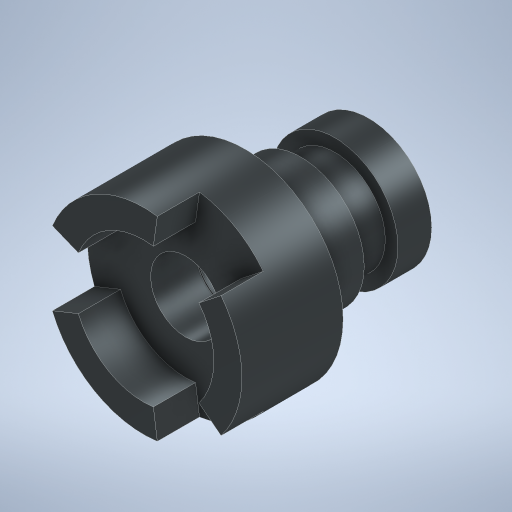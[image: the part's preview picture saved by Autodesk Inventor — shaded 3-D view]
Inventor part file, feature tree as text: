
AUTODESK INVENTOR PART (.ipt)
format: ipt  version: 2023 (Build 270158000, 158)  size: 320,000 bytes
history: native  units: in
note: dims shown in document units (in); Inventor stores cm internally (conversion verified against a paired STEP export)
features: sketch x9, extrude x8
ambient origin geometry x8: Origin, YZ Plane, XZ Plane, XY Plane, X Axis, Y Axis, Z Axis, Center Point
bodies: Solid1 (feature_tree)
feature tree (17):
  extrude  "Extrusion1"  Depth=0.4724in TaperAngle=0.0deg
  extrude  "Extrusion2"  Depth=1.4173in TaperAngle=0.0deg
  extrude  "Extrusion3"  Depth=0.5906in TaperAngle=360.0deg
  extrude  "Extrusion4"  Depth=0.6299in TaperAngle=0.0deg
  extrude  "Extrusion5"  [1 undecoded]
  extrude  "Extrusion6"  [1 undecoded]
  extrude  "Extrusion7"  [1 undecoded]
  sketch  "Sketch8"
  extrude  "Extrusion8"  [1 undecoded]
  sketch  "Sketch1"  dims[d2=0.4724in d3=0.0in d5=0.4724in d6=0.0in]
  sketch  "Sketch2"  dims[d7=0.7874in d8=0.0in d10=1.4173in d11=0.0in]
  sketch  "Sketch3"  dims[d13=0.5906in d14=0.0in d15=1.1811in d17=360.0deg]
  sketch  "Sketch4"  dims[d19=0.5906in d20=0.0in d25=0.6299in d26=0.0in]
  sketch  "Sketch5"  dims[d27=2.0in d28=0.0in]
  sketch  "Sketch6"
  sketch  "Sketch7"
  sketch  "Sketch9"
note: 4 required parameter values undecoded (feature->parameter linkage not recoverable at this tier; creation-order binding heuristic only, values carry confidence <= 0.55)
